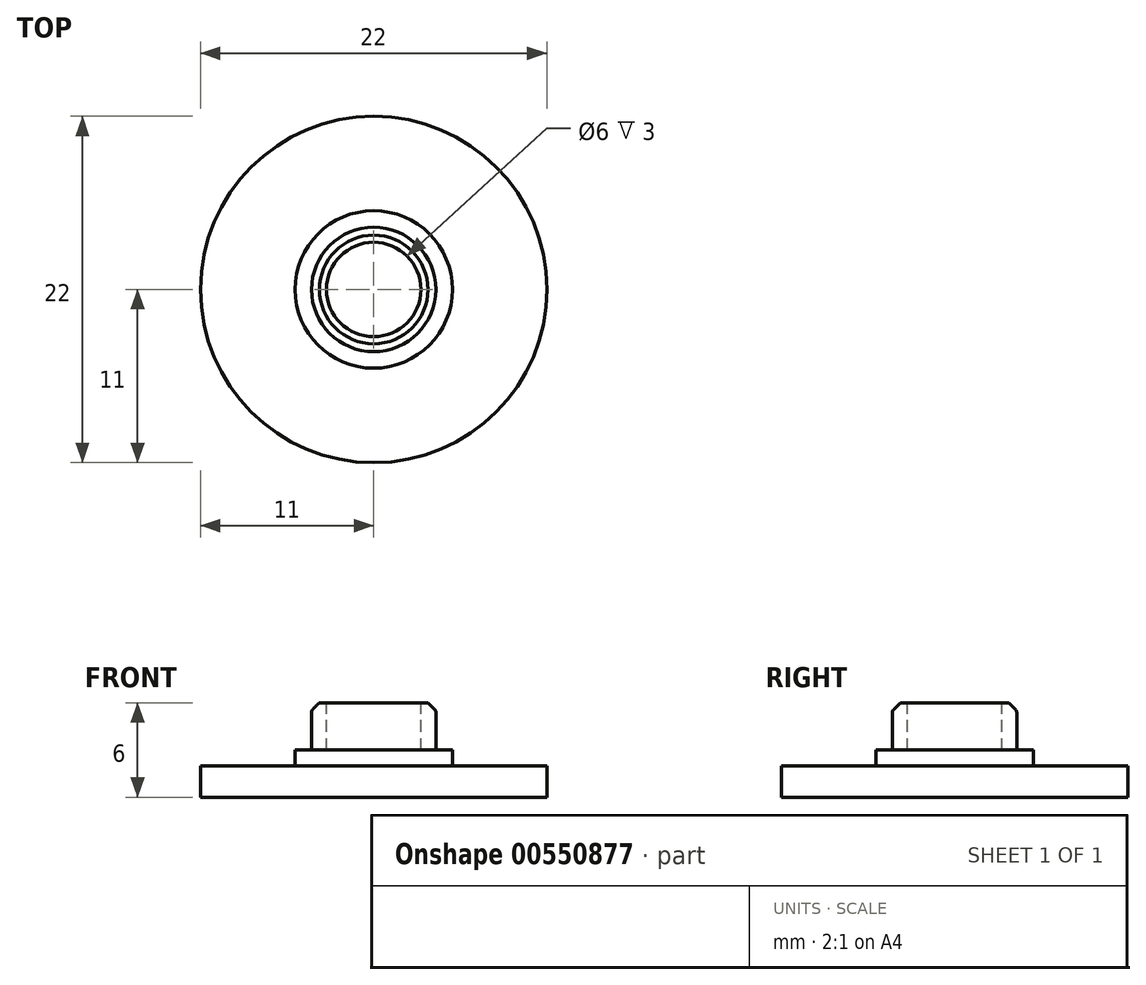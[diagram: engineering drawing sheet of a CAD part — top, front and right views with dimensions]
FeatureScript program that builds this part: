
annotation { "Feature Type Name" : "Feature", "Feature Type Description" : "" }
export const myFeature = defineFeature(function(context is Context, id is Id, definition is map)
    precondition{}
    {
        {
            var Q0;
            Q0=qCreatedBy(makeId("Top.planeOp"),FACE);
            var sketch = newSketch(context, id + "F0", { "sketchPlane" : qUnion([Q0])});
            skCircle(sketch, "E0", {"center": v(0, 0) * mm, "radius": 11 * mm});
            skSolve(sketch);
        }
        {
            var Q0;
            Q0=makeQuery(id+"F0.imprint","IMPRINT",FACE,{"disambiguationData":[TD([[makeQuery(id+"F0.imprint","IMPRINT",EDGE,{"derivedFrom":sQuery(id+"F0.wireOp",EDGE,"E0")}),1.0]])]});
            extrude(context, id + "F1", {"entities" : qUnion([Q0]), "depth" : 2 * mm, "offsetDistance" : 25 * mm});
        }
        {
            var Q0;
            Q0=makeQuery(id+"F1.opExtrude","CAP_FACE",FACE,{"disambiguationData":[OSD([sQuery(id+"F0.wireOp",EDGE,"E0")])],"isStart":false});
            var sketch = newSketch(context, id + "F2", { "sketchPlane" : qUnion([Q0])});
            skCircle(sketch, "E1", {"center": v(0, 0) * mm, "radius": 5 * mm});
            skSolve(sketch);
        }
        {
            var Q0;
            Q0=makeQuery(id+"F2.imprint","IMPRINT",FACE,{"disambiguationData":[TD([[makeQuery(id+"F2.imprint","IMPRINT",EDGE,{"derivedFrom":sQuery(id+"F2.wireOp",EDGE,"E1")}),1.0]])]});
            extrude(context, id + "F3", {"entities" : qUnion([Q0]), "operationType" : NewBodyOperationType.ADD, "depth" : 1 * mm, "offsetDistance" : 25 * mm});
        }
        {
            var Q0;
            Q0=makeQuery(id+"F3.opExtrude","CAP_FACE",FACE,{"disambiguationData":[OSD([sQuery(id+"F2.wireOp",EDGE,"E1")])],"isStart":false});
            var sketch = newSketch(context, id + "F4", { "sketchPlane" : qUnion([Q0])});
            skCircle(sketch, "E2", {"center": v(0, 0) * mm, "radius": 3.95 * mm});
            skSolve(sketch);
        }
        {
            var Q0;
            Q0=makeQuery(id+"F4.imprint","IMPRINT",FACE,{"disambiguationData":[TD([[makeQuery(id+"F4.imprint","IMPRINT",EDGE,{"derivedFrom":sQuery(id+"F4.wireOp",EDGE,"E2")}),1.0]])]});
            extrude(context, id + "F5", {"entities" : qUnion([Q0]), "operationType" : NewBodyOperationType.ADD, "depth" : 3 * mm, "offsetDistance" : 25 * mm});
        }
        {
            var Q0;
            Q0=makeQuery(id+"F5.opExtrude","CAP_FACE",FACE,{"disambiguationData":[OSD([sQuery(id+"F4.wireOp",EDGE,"E2")])],"isStart":false});
            var sketch = newSketch(context, id + "F6", { "sketchPlane" : qUnion([Q0])});
            skCircle(sketch, "E3", {"center": v(0, 0) * mm, "radius": 3 * mm});
            skSolve(sketch);
        }
        {
            var Q0;
            Q0=makeQuery(id+"F6.imprint","IMPRINT",FACE,{"disambiguationData":[TD([[makeQuery(id+"F6.imprint","IMPRINT",EDGE,{"derivedFrom":sQuery(id+"F6.wireOp",EDGE,"E3")}),1.0]])]});
            extrude(context, id + "F7", {"entities" : qUnion([Q0]), "operationType" : NewBodyOperationType.REMOVE, "oppositeDirection" : true, "depth" : 3 * mm, "offsetDistance" : 25 * mm});
        }
        {
            var Q0;
            Q0=makeQuery(id+"F5.opExtrude","CAP_EDGE",EDGE,{"disambiguationData":[OSD([sQuery(id+"F4.wireOp",EDGE,"E2")])],"isStart":false});
            chamfer(context, id + "F8", {"entities" : qUnion([Q0]), "width" : 0.5 * mm, "tangentPropagation" : true});
        }
        {
            var Q0;
            {var subQ0=sQuery(id+"F4.wireOp",EDGE,"E2");Q0=makeQuery(id+"F8.opChamfer","BLEND_EDGE",EDGE,{"blendedFrom":[makeQuery(id+"F5.opExtrude","CAP_EDGE",EDGE,{"disambiguationData":[OSD([subQ0])],"isStart":false}),makeQuery(id+"F5.opExtrude","SWEPT_FACE",FACE,{"disambiguationData":[OSD([subQ0])]})],"blendedInto":[makeQuery(id+"F5.opExtrude","SWEPT_FACE",FACE,{"disambiguationData":[OSD([subQ0])]})]});}
            fillet(context, id + "F9", {"entities" : qUnion([Q0]), "radius" : 0.3 * mm, "tangentPropagation" : true, "allowEdgeOverflow" : false});
        }
    });
